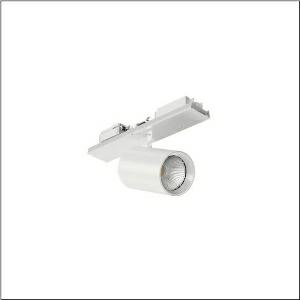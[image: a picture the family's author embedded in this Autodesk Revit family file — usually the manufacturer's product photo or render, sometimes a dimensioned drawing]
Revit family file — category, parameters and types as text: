
# Revit family: licross_r__spot_31_51sl14da35b_dffb
name_source: partatom
category: Lighting Fixtures
units: mm (PartAtom-declared; Revit-internal decimal feet)

## family parameters
Cut with Voids When Loaded = No
Host = Face
Light Source = No
Part Type = Normal
Room Calculation Point = No
Round Connector Dimension = Use Diameter
Shared = No

## types (1)
- --- (1 x LED, 5090 lm, 43.8 W, 3000K)
    Apparent Load = 44 VA
    CIE Flux Codes = 93 97 100 100 100
    Color Rendering = 90
    Color Temperature = 3000K
    Default Elevation = 1800 mm
    Description = Licross® Spot 31, directional spotlight, light control with lens, of plastic, LED rated luminous flux: 5.090lm, light colour: 930, with plug, 5-pole, mains connection: 220..240V, AC, 50/60Hz, of aluminium, traffic white (RAL 9016), length: 300mm, diameter: 90mm, protection rating (complete): IP20, insulation class (complete): insulation class I (protective earthing), certification: CE, packaging unit: 1 piece
    Height = 175 mm
    Lamp = 1 x LED
    Lamp Light Flux = 5090 lm
    Lamp Power = 43.8 W
    Lamp count = 1
    Length = 90 mm
    Luminous efficacy = 116 lm/W
    Manufacturer = Siteco
    ModVariant = No
    Model = 51SL14DA35B
    Mounting Place = Ceiling
    Mounting Type = Pendant
    Number of Poles = 1
    OnlyDefault = Yes
    Power Factor = 1
    Product Name = Licross® Spot 31
    Product group = directional spotlight
    ProductGroupID = 905
    Protection Class = Protection class I
    Protection Degree = IP 20
    RLX_Detail_Level = 1
    RLX_Emergency_Light_Flux = 0 lm
    RLX_Emergency_Type = 0
    RLX_Emergency_Type_DB = No
    RlxData = <blob elided: 14837 chars, md5=14e47bfb>
    Socket = socket
    Standby Power = 0 W
    System Light Flux = 5090 lm
    System Power = 44 W
    Type Comments = factory setting: luminous flux: 100 % | (ON | ON | ON) | 1050 mA
    Type Image = l_1245720.jpg
    URL = http://relux.com
    VarID = @adj_153247
    Voltage = 0 V
    Weight = 0.00 kg
    Width = 0 mm  [stored 0 ft]

note: [stored X ft] marks values corroborated as IEEE doubles in the binary element streams (Revit-internal decimal feet)

## geometry (parser evidence)
native form markers: Sweep x12
no freeform markers — native parametric forms only
